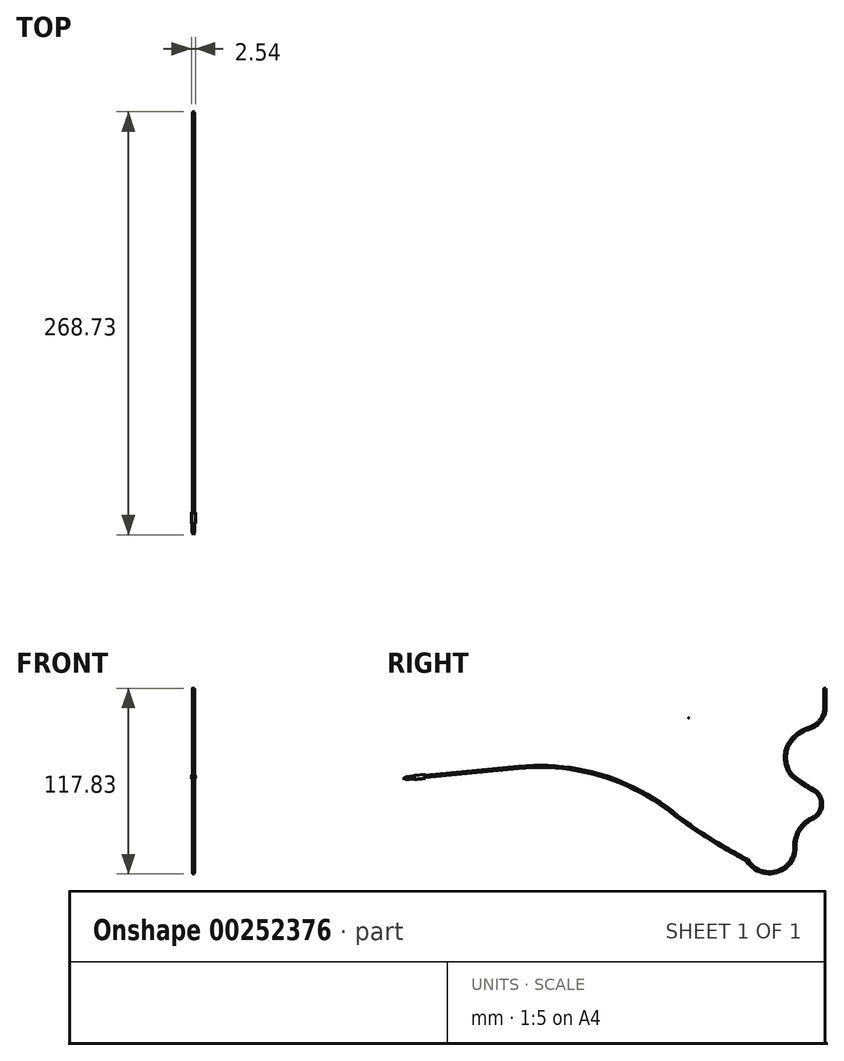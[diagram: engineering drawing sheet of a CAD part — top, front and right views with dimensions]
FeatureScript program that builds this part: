
annotation { "Feature Type Name" : "Feature", "Feature Type Description" : "" }
export const myFeature = defineFeature(function(context is Context, id is Id, definition is map)
    precondition{}
    {
        {
            var Q0;
            Q0=qCreatedBy(makeId("Top.planeOp"),FACE);
            var sketch = newSketch(context, id + "F0", { "sketchPlane" : qUnion([Q0])});
            skCircle(sketch, "E0", {"center": v(0, 0) * mm, "radius": 0.64 * mm});
            skSolve(sketch);
        }
        {
            var Q0;
            Q0=qCreatedBy(makeId("Right.planeOp"),FACE);
            var sketch = newSketch(context, id + "F1", { "sketchPlane" : qUnion([Q0])});
            skLineSegment(sketch, "E1", {"start": v(0, 0) * mm, "end": v(0, -11.85) * mm});
            skArc(sketch, "E2", {"start": v(-10.36, -25.4) * mm, "mid": v(-2.89, -20.37) * mm, "end": v(0, -11.85) * mm});
            skArc(sketch, "E3", {"start": v(-10.36, -25.4) * mm, "mid": v(-18.46, -30.03) * mm, "end": v(-24.12, -37.46) * mm});
            skArc(sketch, "E4", {"start": v(-24.12, -37.46) * mm, "mid": v(-24.93, -46.69) * mm, "end": v(-21.37, -55.24) * mm});
            skArc(sketch, "E5", {"start": v(-21.37, -55.24) * mm, "mid": v(-13.96, -60.62) * mm, "end": v(-6.13, -65.37) * mm});
            skArc(sketch, "E6", {"start": v(-9.2, -83.15) * mm, "mid": v(-2.35, -75.17) * mm, "end": v(-6.13, -65.37) * mm});
            skArc(sketch, "E7", {"start": v(-9.2, -83.15) * mm, "mid": v(-17.12, -91.37) * mm, "end": v(-19.04, -102.62) * mm});
            skArc(sketch, "E8", {"start": v(-93.74, -81.41) * mm, "mid": v(-141.12, -55.67) * mm, "end": v(-194.76, -50.2) * mm});
            skLineSegment(sketch, "E9", {"start": v(-194.76, -50.2) * mm, "end": v(-254, -55.93) * mm});
            skArc(sketch, "E10", {"start": v(-93.74, -81.41) * mm, "mid": v(-72.19, -96.16) * mm, "end": v(-49.53, -109.15) * mm});
            skArc(sketch, "E11", {"start": v(-49.53, -109.15) * mm, "mid": v(-31.94, -116.84) * mm, "end": v(-19.04, -102.62) * mm});
            skSolve(sketch);
        }
        {
            var Q0;
            Q0=makeQuery(id+"F0.imprint","IMPRINT",FACE,{"disambiguationData":[TD([[makeQuery(id+"F0.imprint","IMPRINT",EDGE,{"derivedFrom":sQuery(id+"F0.wireOp",EDGE,"E0")}),1.0]])]});
            var Q1;
            Q1=sQuery(id+"F1.wireOp",EDGE,"E9");
            var Q2;
            Q2=sQuery(id+"F1.wireOp",EDGE,"E8");
            var Q3;
            Q3=sQuery(id+"F1.wireOp",EDGE,"E10");
            var Q4;
            Q4=sQuery(id+"F1.wireOp",EDGE,"E11");
            var Q5;
            Q5=sQuery(id+"F1.wireOp",EDGE,"E7");
            var Q6;
            Q6=sQuery(id+"F1.wireOp",EDGE,"E6");
            var Q7;
            Q7=sQuery(id+"F1.wireOp",EDGE,"E5");
            var Q8;
            Q8=sQuery(id+"F1.wireOp",EDGE,"E4");
            var Q9;
            Q9=sQuery(id+"F1.wireOp",EDGE,"E3");
            var Q10;
            Q10=sQuery(id+"F1.wireOp",EDGE,"E2");
            var Q11;
            Q11=sQuery(id+"F1.wireOp",EDGE,"E1");
            sweep(context, id + "F2", {"profiles" : qUnion([Q0]), "path" : qUnion([Q1, Q2, Q3, Q4, Q5, Q6, Q7, Q8, Q9, Q10, Q11])});
        }
        {
            var Q0;
            Q0=makeQuery(id+"F2.opSweep","CAP_FACE",FACE,{"disambiguationData":[OSD([sQuery(id+"F0.wireOp",EDGE,"E0"),sQuery(id+"F1.wireOp",VERTEX,"E9.end")])],"isStart":false});
            var sketch = newSketch(context, id + "F3", { "sketchPlane" : qUnion([Q0])});
            skCircle(sketch, "E12", {"center": v(0, -31.2) * mm, "radius": 1.27 * mm});
            skSolve(sketch);
        }
        {
            var Q0;
            Q0=qSketchRegion(id+"F3",true);
            extrude(context, id + "F4", {"entities" : qUnion([Q0]), "operationType" : NewBodyOperationType.ADD, "depth" : 6.8 * mm});
        }
        {
            var Q0;
            Q0=qCreatedBy(makeId("Right.planeOp"),FACE);
            var sketch = newSketch(context, id + "F5", { "sketchPlane" : qUnion([Q0])});
            skLineSegment(sketch, "E13", {"start": v(-86.87, -18.84) * mm, "end": v(-86.53, -18.8) * mm});
            skLineSegment(sketch, "E14", {"start": v(-86.53, -18.8) * mm, "end": v(-86.54, -18.73) * mm});
            skLineSegment(sketch, "E15", {"start": v(-86.54, -18.73) * mm, "end": v(-86.87, -18.84) * mm});
            skSolve(sketch);
        }
        {
            var Q0;
            Q0=makeQuery(id+"F5.imprint","IMPRINT",FACE,{"disambiguationData":[TD([[makeQuery(id+"F5.imprint","IMPRINT",EDGE,{"derivedFrom":sQuery(id+"F5.wireOp",EDGE,"E13")}),1.0]])]});
            var Q1;
            Q1=sQuery(id+"F5.wireOp",EDGE,"E13");
            revolve(context, id + "F6", {"operationType" : NewBodyOperationType.ADD, "entities" : qUnion([Q0]), "axis" : qUnion([Q1]), "revolveType" : RevolveType.FULL});
        }
        {
            var Q0;
            Q0=qCreatedBy(makeId("Right.planeOp"),FACE);
            var sketch = newSketch(context, id + "F7", { "sketchPlane" : qUnion([Q0])});
            skLineSegment(sketch, "E16", {"start": v(-266.1, -57.11) * mm, "end": v(-266, -57.84) * mm});
            skLineSegment(sketch, "E17", {"start": v(-266, -57.84) * mm, "end": v(-268.1, -57.33) * mm});
            skLineSegment(sketch, "E18", {"start": v(-268.1, -57.33) * mm, "end": v(-266.1, -57.11) * mm});
            skLineSegment(sketch, "E19", {"start": v(-266.1, -57.11) * mm, "end": v(-260.77, -56.59) * mm});
            skLineSegment(sketch, "E20", {"start": v(-260.77, -56.59) * mm, "end": v(-260.66, -57.41) * mm});
            skLineSegment(sketch, "E21", {"start": v(-266, -57.84) * mm, "end": v(-260.66, -57.41) * mm, "construction": true});
            skLineSegment(sketch, "E22", {"start": v(-266, -57.84) * mm, "end": v(-265.21, -57.78) * mm});
            skLineSegment(sketch, "E23", {"start": v(-265.21, -57.78) * mm, "end": v(-265.22, -57.65) * mm});
            skLineSegment(sketch, "E24", {"start": v(-265.22, -57.65) * mm, "end": v(-264.88, -57.62) * mm});
            skLineSegment(sketch, "E25", {"start": v(-264.88, -57.62) * mm, "end": v(-264.87, -57.75) * mm});
            skLineSegment(sketch, "E26", {"start": v(-264.87, -57.75) * mm, "end": v(-263.7, -57.66) * mm});
            skLineSegment(sketch, "E27", {"start": v(-263.7, -57.66) * mm, "end": v(-263.71, -57.52) * mm});
            skLineSegment(sketch, "E28", {"start": v(-263.71, -57.52) * mm, "end": v(-263.47, -57.5) * mm});
            skLineSegment(sketch, "E29", {"start": v(-263.47, -57.5) * mm, "end": v(-263.46, -57.64) * mm});
            skLineSegment(sketch, "E30", {"start": v(-263.46, -57.64) * mm, "end": v(-262.16, -57.53) * mm});
            skLineSegment(sketch, "E31", {"start": v(-262.16, -57.53) * mm, "end": v(-262.17, -57.41) * mm});
            skLineSegment(sketch, "E32", {"start": v(-262.17, -57.41) * mm, "end": v(-261.94, -57.4) * mm});
            skLineSegment(sketch, "E33", {"start": v(-261.94, -57.4) * mm, "end": v(-261.93, -57.51) * mm});
            skLineSegment(sketch, "E34", {"start": v(-261.93, -57.51) * mm, "end": v(-260.66, -57.41) * mm});
            skSolve(sketch);
        }
        {
            var Q0;
            Q0=qSketchRegion(id+"F7",true);
            var Q1;
            Q1=sQuery(id+"F7.wireOp",EDGE,"E18");
            revolve(context, id + "F8", {"operationType" : NewBodyOperationType.ADD, "entities" : qUnion([Q0]), "axis" : qUnion([Q1]), "revolveType" : RevolveType.FULL});
        }
    });
